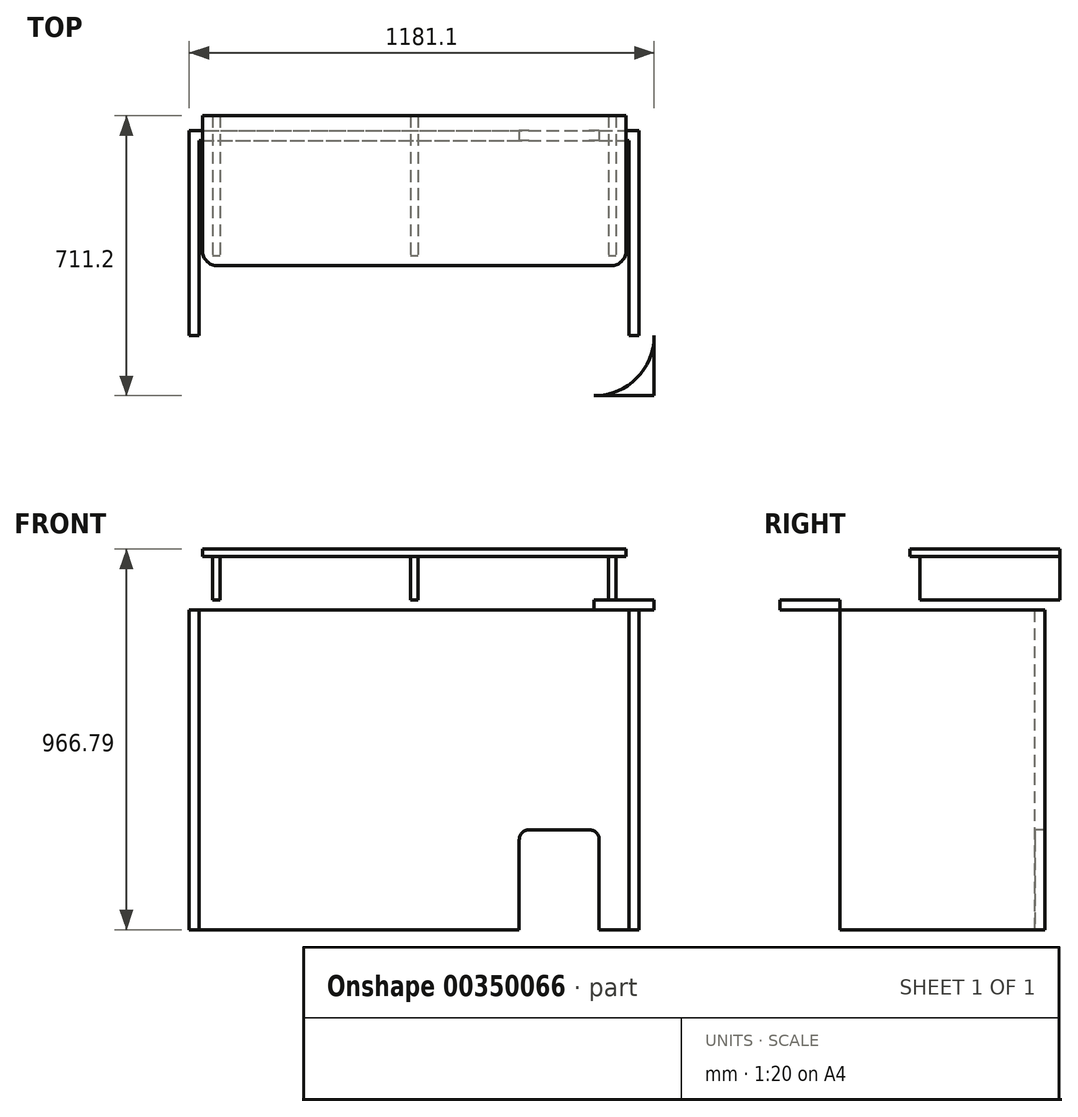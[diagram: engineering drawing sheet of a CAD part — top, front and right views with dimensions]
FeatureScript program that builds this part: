
annotation { "Feature Type Name" : "Feature", "Feature Type Description" : "" }
export const myFeature = defineFeature(function(context is Context, id is Id, definition is map)
    precondition{}
    {
        {
            var Q0;
            Q0=qCreatedBy(makeId("Top.planeOp"),FACE);
            var sketch = newSketch(context, id + "F0", { "sketchPlane" : qUnion([Q0])});
            skLineSegment(sketch, "E0.bottom", {"start": v(0, 0) * mm, "end": v(1219.2, 0) * mm});
            skLineSegment(sketch, "E0.top", {"start": v(0, 711.2) * mm, "end": v(1219.2, 711.2) * mm});
            skLineSegment(sketch, "E0.left", {"start": v(0, 0) * mm, "end": v(0, 711.2) * mm});
            skLineSegment(sketch, "E0.right", {"start": v(1219.2, 0) * mm, "end": v(1219.2, 711.2) * mm});
            skSolve(sketch);
        }
        {
            var Q0;
            Q0=makeQuery(id+"F0.imprint","IMPRINT",FACE,{"disambiguationData":[TD([[makeQuery(id+"F0.imprint","IMPRINT",EDGE,{"derivedFrom":sQuery(id+"F0.wireOp",EDGE,"E0.bottom")}),1.0]])]});
            extrude(context, id + "F1", {"entities" : qUnion([Q0]), "depth" : 25.4 * mm});
        }
        {
            var Q0;
            Q0=makeQuery(id+"F1.opExtrude","CAP_FACE",FACE,{"disambiguationData":[OSD([sQuery(id+"F0.wireOp",EDGE,"E0.bottom"),sQuery(id+"F0.wireOp",EDGE,"E0.top"),sQuery(id+"F0.wireOp",EDGE,"E0.left"),sQuery(id+"F0.wireOp",EDGE,"E0.right")])],"isStart":false});
            var sketch = newSketch(context, id + "F2", { "sketchPlane" : qUnion([Q0])});
            skArc(sketch, "E1", {"start": v(0, 152.4) * mm, "mid": v(44.64, 44.64) * mm, "end": v(152.4, 0) * mm});
            skLineSegment(sketch, "E2", {"start": v(609.6, 0) * mm, "end": v(609.6, 711.2) * mm, "construction": true});
            skArc(sketch, "E3.MirrorCS", {"start": v(1219.2, 152.4) * mm, "mid": v(1174.56, 44.64) * mm, "end": v(1066.8, 0) * mm});
            skSolve(sketch);
        }
        {
            var Q0;
            {var subQ0=sQuery(id+"F2.wireOp",EDGE,"E1");Q0=makeQuery(id+"F2.imprint","IMPRINT",FACE,{"disambiguationData":[TD([[makeQuery(id+"F2.imprint","IMPRINT",EDGE,{"derivedFrom":subQ0}),-1.0]])]});}
            var Q1;
            {var subQ0=sQuery(id+"F2.wireOp",EDGE,"E3.MirrorCS");Q1=makeQuery(id+"F2.imprint","IMPRINT",FACE,{"disambiguationData":[TD([[makeQuery(id+"F2.imprint","IMPRINT",EDGE,{"derivedFrom":subQ0}),1.0]])]});}
            extrude(context, id + "F3", {"entities" : qUnion([Q0, Q1]), "operationType" : NewBodyOperationType.REMOVE, "oppositeDirection" : true, "depth" : 25.4 * mm});
        }
        {
            var Q0;
            Q0=makeQuery(id+"F1.opExtrude","CAP_FACE",FACE,{"disambiguationData":[OSD([sQuery(id+"F0.wireOp",EDGE,"E0.bottom"),sQuery(id+"F0.wireOp",EDGE,"E0.top"),sQuery(id+"F0.wireOp",EDGE,"E0.left"),sQuery(id+"F0.wireOp",EDGE,"E0.right")])],"isStart":false});
            var sketch = newSketch(context, id + "F4", { "sketchPlane" : qUnion([Q0])});
            skLineSegment(sketch, "E4.bottom", {"start": v(96.84, 711.2) * mm, "end": v(115.89, 711.2) * mm});
            skLineSegment(sketch, "E4.top", {"start": v(96.84, 355.6) * mm, "end": v(115.89, 355.6) * mm});
            skLineSegment(sketch, "E4.left", {"start": v(96.84, 711.2) * mm, "end": v(96.84, 355.6) * mm});
            skLineSegment(sketch, "E4.right", {"start": v(115.89, 711.2) * mm, "end": v(115.89, 355.6) * mm});
            skLineSegment(sketch, "E5.bottom", {"start": v(600.07, 711.2) * mm, "end": v(619.12, 711.2) * mm});
            skLineSegment(sketch, "E5.top", {"start": v(600.07, 355.6) * mm, "end": v(619.12, 355.6) * mm});
            skLineSegment(sketch, "E5.left", {"start": v(600.07, 711.2) * mm, "end": v(600.07, 355.6) * mm});
            skLineSegment(sketch, "E5.right", {"start": v(619.12, 711.2) * mm, "end": v(619.12, 355.6) * mm});
            skLineSegment(sketch, "E6.bottom", {"start": v(1103.31, 711.2) * mm, "end": v(1122.36, 711.2) * mm});
            skLineSegment(sketch, "E6.top", {"start": v(1103.31, 355.6) * mm, "end": v(1122.36, 355.6) * mm});
            skLineSegment(sketch, "E6.left", {"start": v(1103.31, 711.2) * mm, "end": v(1103.31, 355.6) * mm});
            skLineSegment(sketch, "E6.right", {"start": v(1122.36, 711.2) * mm, "end": v(1122.36, 355.6) * mm});
            skLineSegment(sketch, "E7", {"start": v(96.84, 355.6) * mm, "end": v(0, 355.6) * mm, "construction": true});
            skLineSegment(sketch, "E8", {"start": v(1122.36, 355.6) * mm, "end": v(1219.2, 355.6) * mm, "construction": true});
            skSolve(sketch);
        }
        {
            var Q0;
            Q0=makeQuery(id+"F4.imprint","IMPRINT",FACE,{"disambiguationData":[TD([[makeQuery(id+"F4.imprint","IMPRINT",EDGE,{"derivedFrom":sQuery(id+"F4.wireOp",EDGE,"8PtXw70h-2QZq-hl5j-LBv2-GIjZ8nnPCKIa.bottom")}),-1.0]])]});
            var Q1;
            Q1=makeQuery(id+"F4.imprint","IMPRINT",FACE,{"disambiguationData":[TD([[makeQuery(id+"F4.imprint","IMPRINT",EDGE,{"derivedFrom":sQuery(id+"F4.wireOp",EDGE,"E4.bottom")}),-1.0]])]});
            var Q2;
            Q2=makeQuery(id+"F4.imprint","IMPRINT",FACE,{"disambiguationData":[TD([[makeQuery(id+"F4.imprint","IMPRINT",EDGE,{"derivedFrom":sQuery(id+"F4.wireOp",EDGE,"90c45b21-91bc-413f-b475-0f41eeefe8540.MirrorCS")}),-1.0]])]});
            var Q3;
            Q3=makeQuery(id+"F4.imprint","IMPRINT",FACE,{"disambiguationData":[TD([[makeQuery(id+"F4.imprint","IMPRINT",EDGE,{"derivedFrom":sQuery(id+"F4.wireOp",EDGE,"dfd83140-ed69-49ea-8c0d-0c25f39699ef0.MirrorCS")}),-1.0]])]});
            var Q4;
            Q4=makeQuery(id+"F4.imprint","IMPRINT",FACE,{"disambiguationData":[TD([[makeQuery(id+"F4.imprint","IMPRINT",EDGE,{"derivedFrom":sQuery(id+"F4.wireOp",EDGE,"E5.bottom")}),-1.0]])]});
            var Q5;
            Q5=makeQuery(id+"F4.imprint","IMPRINT",FACE,{"disambiguationData":[TD([[makeQuery(id+"F4.imprint","IMPRINT",EDGE,{"derivedFrom":sQuery(id+"F4.wireOp",EDGE,"E6.bottom")}),-1.0]])]});
            extrude(context, id + "F5", {"entities" : qUnion([Q0, Q1, Q2, Q3, Q4, Q5]), "depth" : 109.54 * mm});
        }
        {
            var Q0;
            Q0=makeQuery(id+"F1.opExtrude","CAP_FACE",FACE,{"disambiguationData":[OSD([sQuery(id+"F0.wireOp",EDGE,"E0.bottom"),sQuery(id+"F0.wireOp",EDGE,"E0.top"),sQuery(id+"F0.wireOp",EDGE,"E0.left"),sQuery(id+"F0.wireOp",EDGE,"E0.right")])],"isStart":true});
            var sketch = newSketch(context, id + "F6", { "sketchPlane" : qUnion([Q0])});
            skLineSegment(sketch, "E9.bottom", {"start": v(38.1, -152.4) * mm, "end": v(63.5, -152.4) * mm});
            skLineSegment(sketch, "E9.top", {"start": v(38.1, -673.1) * mm, "end": v(63.5, -673.1) * mm});
            skLineSegment(sketch, "E9.left", {"start": v(38.1, -152.4) * mm, "end": v(38.1, -673.1) * mm});
            skLineSegment(sketch, "E9.right", {"start": v(63.5, -152.4) * mm, "end": v(63.5, -673.1) * mm});
            skLineSegment(sketch, "E10.bottom", {"start": v(63.5, -673.1) * mm, "end": v(1155.7, -673.1) * mm});
            skLineSegment(sketch, "E10.top", {"start": v(63.5, -647.7) * mm, "end": v(1155.7, -647.7) * mm});
            skLineSegment(sketch, "E10.left", {"start": v(63.5, -673.1) * mm, "end": v(63.5, -647.7) * mm});
            skLineSegment(sketch, "E10.right", {"start": v(1155.7, -673.1) * mm, "end": v(1155.7, -647.7) * mm});
            skLineSegment(sketch, "E11.bottom", {"start": v(1155.7, -673.1) * mm, "end": v(1181.1, -673.1) * mm});
            skLineSegment(sketch, "E11.top", {"start": v(1155.7, -152.4) * mm, "end": v(1181.1, -152.4) * mm});
            skLineSegment(sketch, "E11.left", {"start": v(1155.7, -673.1) * mm, "end": v(1155.7, -152.4) * mm});
            skLineSegment(sketch, "E11.right", {"start": v(1181.1, -673.1) * mm, "end": v(1181.1, -152.4) * mm});
            skSolve(sketch);
        }
        {
            var Q0;
            Q0 = qSketchRegion(id + "F6", true);
            extrude(context, id + "F7", {"entities" : qUnion([Q0]), "depth" : 812.8 * mm});
        }
        {
            var Q0;
            Q0=makeQuery(id+"F5.opExtrude","CAP_FACE",FACE,{"disambiguationData":[OSD([sQuery(id+"F4.wireOp",EDGE,"E4.bottom"),sQuery(id+"F4.wireOp",EDGE,"E4.top"),sQuery(id+"F4.wireOp",EDGE,"E4.left"),sQuery(id+"F4.wireOp",EDGE,"E4.right")])],"isStart":false});
            var sketch = newSketch(context, id + "F8", { "sketchPlane" : qUnion([Q0])});
            skLineSegment(sketch, "E12.bottom", {"start": v(71.44, 711.2) * mm, "end": v(1147.76, 711.2) * mm});
            skLineSegment(sketch, "E12.top", {"start": v(71.44, 330.2) * mm, "end": v(1147.76, 330.2) * mm});
            skLineSegment(sketch, "E12.left", {"start": v(71.44, 711.2) * mm, "end": v(71.44, 330.2) * mm});
            skLineSegment(sketch, "E12.right", {"start": v(1147.76, 711.2) * mm, "end": v(1147.76, 330.2) * mm});
            skSolve(sketch);
        }
        {
            var Q0;
            {var subQ2=sQuery(id+"F8.wireOp",EDGE,"E12.right");Q0=makeQuery(id+"F8.imprint","IMPRINT",FACE,{"disambiguationData":[TD([[makeQuery(id+"F8.imprint","IMPRINT",EDGE,{"derivedFrom":subQ2}),-1.0]])]});}
            var Q1;
            {var subQ2=sQuery(id+"F8.wireOp",EDGE,"E12.left");Q1=makeQuery(id+"F8.imprint","IMPRINT",FACE,{"disambiguationData":[TD([[makeQuery(id+"F8.imprint","IMPRINT",EDGE,{"derivedFrom":subQ2}),1.0]])]});}
            var Q2;
            {var subQ1=makeQuery(id+"F5.opExtrude","CAP_EDGE",EDGE,{"disambiguationData":[OSD([sQuery(id+"F4.wireOp",EDGE,"E4.left")])],"isStart":false});Q2=makeQuery(id+"F8.imprint","IMPRINT",FACE,{"disambiguationData":[TD([[makeQuery(id+"F8.imprint","IMPRINT",EDGE,{"derivedFrom":subQ1}),1.0]])]});}
            extrude(context, id + "F9", {"entities" : qUnion([Q0, Q1, Q2]), "depth" : 19.05 * mm});
        }
        {
            var Q0;
            Q0=makeQuery(id+"F9.opExtrude","SWEPT_EDGE",EDGE,{"disambiguationData":[OSD([sQuery(id+"F8.wireOp",EDGE,"E12.top"),sQuery(id+"F8.wireOp",EDGE,"E12.left")])]});
            var Q1;
            Q1=makeQuery(id+"F9.opExtrude","SWEPT_EDGE",EDGE,{"disambiguationData":[OSD([sQuery(id+"F8.wireOp",EDGE,"E12.top"),sQuery(id+"F8.wireOp",EDGE,"E12.right")])]});
            fillet(context, id + "F10", {"entities" : qUnion([Q0, Q1]), "radius" : 38.1 * mm, "tangentPropagation" : true, "allowEdgeOverflow" : false});
        }
        {
            var Q0;
            Q0=makeQuery(id+"F7.opExtrude","SWEPT_FACE",FACE,{"disambiguationData":[OSD([sQuery(id+"F6.wireOp",EDGE,"E10.top")])]});
            var sketch = newSketch(context, id + "F11", { "sketchPlane" : qUnion([Q0])});
            skLineSegment(sketch, "E13.bottom", {"start": v(876.3, -558.8) * mm, "end": v(1079.5, -558.8) * mm});
            skLineSegment(sketch, "E13.top", {"start": v(876.3, -812.8) * mm, "end": v(1079.5, -812.8) * mm});
            skLineSegment(sketch, "E13.left", {"start": v(876.3, -558.8) * mm, "end": v(876.3, -812.8) * mm});
            skLineSegment(sketch, "E13.right", {"start": v(1079.5, -558.8) * mm, "end": v(1079.5, -812.8) * mm});
            skSolve(sketch);
        }
        {
            var Q0;
            Q0 = qSketchRegion(id + "F11", true);
            extrude(context, id + "F12", {"entities" : qUnion([Q0]), "operationType" : NewBodyOperationType.REMOVE, "oppositeDirection" : true, "depth" : 25.4 * mm});
        }
        {
            var Q0;
            Q0=makeQuery(id+"F12.boolean.opBoolean","COPY",EDGE,{"derivedFrom":makeQuery(id+"F12.opExtrude","SWEPT_EDGE",EDGE,{"disambiguationData":[OSD([sQuery(id+"F11.wireOp",EDGE,"E13.bottom"),sQuery(id+"F11.wireOp",EDGE,"E13.right")])]})});
            var Q1;
            Q1=makeQuery(id+"F12.boolean.opBoolean","COPY",EDGE,{"derivedFrom":makeQuery(id+"F12.opExtrude","SWEPT_EDGE",EDGE,{"disambiguationData":[OSD([sQuery(id+"F11.wireOp",EDGE,"E13.bottom"),sQuery(id+"F11.wireOp",EDGE,"E13.left")])]})});
            fillet(context, id + "F13", {"entities" : qUnion([Q0, Q1]), "radius" : 25.4 * mm, "tangentPropagation" : true, "allowEdgeOverflow" : false});
        }
    });
